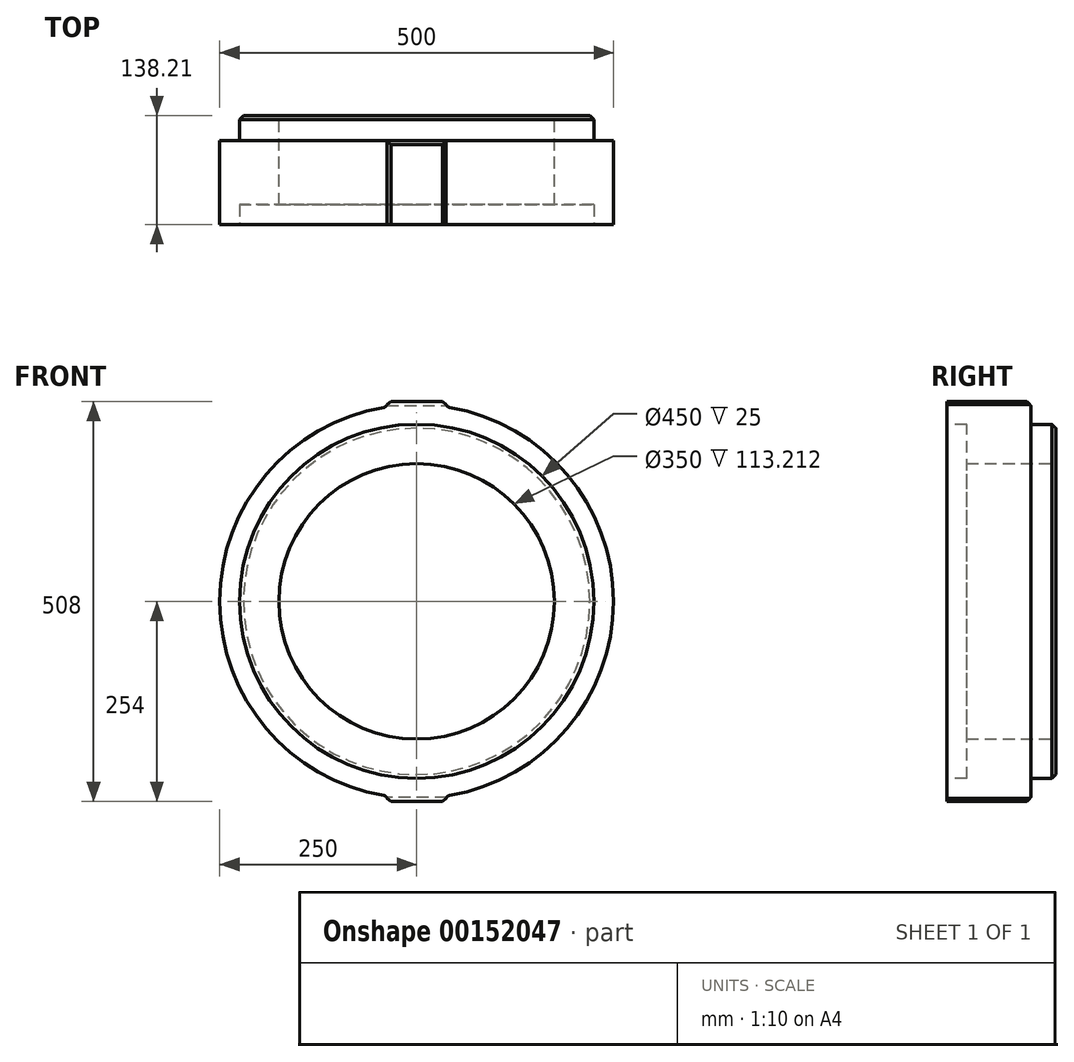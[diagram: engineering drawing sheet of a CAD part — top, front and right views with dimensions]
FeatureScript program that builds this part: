
annotation { "Feature Type Name" : "Feature", "Feature Type Description" : "" }
export const myFeature = defineFeature(function(context is Context, id is Id, definition is map)
    precondition{}
    {
        {
            var Q0;
            Q0=qCreatedBy(makeId("Front.planeOp"),FACE);
            var sketch = newSketch(context, id + "F0", { "sketchPlane" : qUnion([Q0])});
            skArc(sketch, "E0", {"start": v(37.5, -247.17) * mm, "mid": v(250, 0) * mm, "end": v(37.5, 247.17) * mm});
            skLineSegment(sketch, "E1.bottom", {"start": v(37.5, 254) * mm, "end": v(-37.5, 254) * mm});
            skLineSegment(sketch, "E1.top", {"start": v(37.5, -254) * mm, "end": v(-37.5, -254) * mm});
            skLineSegment(sketch, "E1.left", {"start": v(37.5, 254) * mm, "end": v(37.5, 247.17) * mm});
            skLineSegment(sketch, "E1.right", {"start": v(-37.5, 254) * mm, "end": v(-37.5, 247.17) * mm});
            skCircle(sketch, "E2", {"center": v(0, 0) * mm, "radius": 175 * mm});
            skLineSegment(sketch, "E3.trimOffspring", {"start": v(37.5, -247.17) * mm, "end": v(37.5, -254) * mm});
            skLineSegment(sketch, "E4.trimOffspring", {"start": v(-37.5, -247.17) * mm, "end": v(-37.5, -254) * mm});
            skArc(sketch, "E5.trimOffspring", {"start": v(-37.5, 247.17) * mm, "mid": v(-250, 0) * mm, "end": v(-37.5, -247.17) * mm});
            skSolve(sketch);
        }
        {
            var Q0;
            Q0 = qSketchRegion(id + "F0", true);
            extrude(context, id + "F1", {"entities" : qUnion([Q0]), "depth" : 150 * mm});
        }
        {
            var Q0;
            Q0=makeQuery(id+"F1.opExtrude","CAP_FACE",FACE,{"disambiguationData":[OSD([sQuery(id+"F0.wireOp",EDGE,"E0"),sQuery(id+"F0.wireOp",EDGE,"E1.bottom"),sQuery(id+"F0.wireOp",EDGE,"E1.top"),sQuery(id+"F0.wireOp",EDGE,"E1.left"),sQuery(id+"F0.wireOp",EDGE,"E1.right"),sQuery(id+"F0.wireOp",EDGE,"E2"),sQuery(id+"F0.wireOp",EDGE,"E3.trimOffspring"),sQuery(id+"F0.wireOp",EDGE,"E4.trimOffspring"),sQuery(id+"F0.wireOp",EDGE,"E5.trimOffspring")])],"isStart":false});
            var sketch = newSketch(context, id + "F2", { "sketchPlane" : qUnion([Q0])});
            skCircle(sketch, "E6", {"center": v(0, 0) * mm, "radius": 225 * mm});
            skCircle(sketch, "E7", {"center": v(0, 0) * mm, "radius": 175 * mm});
            skSolve(sketch);
        }
        {
            var Q0;
            Q0 = qSketchRegion(id + "F2", true);
            extrude(context, id + "F3", {"entities" : qUnion([Q0]), "operationType" : NewBodyOperationType.REMOVE, "oppositeDirection" : true, "depth" : 25 * mm});
        }
        {
            var Q0;
            Q0=makeQuery(id+"F1.opExtrude","CAP_FACE",FACE,{"disambiguationData":[OSD([sQuery(id+"F0.wireOp",EDGE,"E0"),sQuery(id+"F0.wireOp",EDGE,"E1.bottom"),sQuery(id+"F0.wireOp",EDGE,"E1.top"),sQuery(id+"F0.wireOp",EDGE,"E1.left"),sQuery(id+"F0.wireOp",EDGE,"E1.right"),sQuery(id+"F0.wireOp",EDGE,"E2"),sQuery(id+"F0.wireOp",EDGE,"E3.trimOffspring"),sQuery(id+"F0.wireOp",EDGE,"E4.trimOffspring"),sQuery(id+"F0.wireOp",EDGE,"E5.trimOffspring")])],"isStart":true});
            var sketch = newSketch(context, id + "F4", { "sketchPlane" : qUnion([Q0])});
            skCircle(sketch, "E8", {"center": v(0, 0) * mm, "radius": 175 * mm});
            skCircle(sketch, "E9", {"center": v(0, 0) * mm, "radius": 225 * mm});
            skSolve(sketch);
        }
        {
            var Q0;
            Q0 = qSketchRegion(id + "F4", true);
            extrude(context, id + "F5", {"entities" : qUnion([Q0]), "operationType" : NewBodyOperationType.ADD, "depth" : 32 * mm});
        }
        {
            var Q0;
            Q0=makeQuery(id+"F5.opExtrude","CAP_EDGE",EDGE,{"disambiguationData":[OSD([sQuery(id+"F4.wireOp",EDGE,"E9")])],"isStart":false});
            chamfer(context, id + "F6", {"entities" : qUnion([Q0]), "width" : 5 * mm, "tangentPropagation" : true});
        }
        {
            var Q0;
            Q0=makeQuery(id+"F1.opExtrude","SWEPT_EDGE",EDGE,{"disambiguationData":[OSD([sQuery(id+"F0.wireOp",EDGE,"E1.right"),sQuery(id+"F0.wireOp",EDGE,"E5.trimOffspring")])]});
            var Q1;
            Q1=makeQuery(id+"F1.opExtrude","SWEPT_EDGE",EDGE,{"disambiguationData":[OSD([sQuery(id+"F0.wireOp",EDGE,"E0"),sQuery(id+"F0.wireOp",EDGE,"E1.left")])]});
            var Q2;
            Q2=makeQuery(id+"F1.opExtrude","SWEPT_EDGE",EDGE,{"disambiguationData":[OSD([sQuery(id+"F0.wireOp",EDGE,"E4.trimOffspring"),sQuery(id+"F0.wireOp",EDGE,"E5.trimOffspring")])]});
            var Q3;
            Q3=makeQuery(id+"F1.opExtrude","SWEPT_EDGE",EDGE,{"disambiguationData":[OSD([sQuery(id+"F0.wireOp",EDGE,"E0"),sQuery(id+"F0.wireOp",EDGE,"E3.trimOffspring")])]});
            fillet(context, id + "F7", {"entities" : qUnion([Q0, Q1, Q2, Q3]), "radius" : 5 * mm, "tangentPropagation" : true, "allowEdgeOverflow" : false});
        }
        {
            var Q0;
            Q0=makeQuery(id+"F3.boolean.opBoolean","COPY",FACE,{"derivedFrom":makeQuery(id+"F3.opExtrude","CAP_FACE",FACE,{"disambiguationData":[OSD([sQuery(id+"F2.wireOp",EDGE,"E6"),sQuery(id+"F2.wireOp",EDGE,"E7")])],"isStart":false})});
            extrude(context, id + "F8", {"entities" : qUnion([Q0]), "operationType" : NewBodyOperationType.REMOVE, "oppositeDirection" : true, "depth" : 43.8 * mm});
        }
        {
            var Q0;
            Q0=makeQuery(id+"F1.opExtrude","CAP_FACE",FACE,{"disambiguationData":[OSD([sQuery(id+"F0.wireOp",EDGE,"E0"),sQuery(id+"F0.wireOp",EDGE,"E1.bottom"),sQuery(id+"F0.wireOp",EDGE,"E1.top"),sQuery(id+"F0.wireOp",EDGE,"E1.left"),sQuery(id+"F0.wireOp",EDGE,"E1.right"),sQuery(id+"F0.wireOp",EDGE,"E2"),sQuery(id+"F0.wireOp",EDGE,"E3.trimOffspring"),sQuery(id+"F0.wireOp",EDGE,"E4.trimOffspring"),sQuery(id+"F0.wireOp",EDGE,"E5.trimOffspring")])],"isStart":false});
            extrude(context, id + "F9", {"entities" : qUnion([Q0]), "operationType" : NewBodyOperationType.REMOVE, "oppositeDirection" : true, "depth" : 43.8 * mm});
        }
        {
            var Q0;
            Q0=makeQuery(id+"F1.opExtrude","SWEPT_EDGE",EDGE,{"disambiguationData":[OSD([sQuery(id+"F0.wireOp",EDGE,"E1.bottom"),sQuery(id+"F0.wireOp",EDGE,"E1.right")])]});
            var Q1;
            Q1=makeQuery(id+"F1.opExtrude","SWEPT_EDGE",EDGE,{"disambiguationData":[OSD([sQuery(id+"F0.wireOp",EDGE,"E1.bottom"),sQuery(id+"F0.wireOp",EDGE,"E1.left")])]});
            var Q2;
            Q2=makeQuery(id+"F1.opExtrude","CAP_EDGE",EDGE,{"disambiguationData":[OSD([sQuery(id+"F0.wireOp",EDGE,"E1.bottom")])],"isStart":true});
            var Q3;
            Q3=makeQuery(id+"F9.boolean.opBoolean","COPY",EDGE,{"derivedFrom":makeQuery(id+"F9.opExtrude","CAP_EDGE",EDGE,{"disambiguationData":[OSD([sQuery(id+"F0.wireOp",EDGE,"E1.bottom")])],"isStart":false})});
            chamfer(context, id + "F10", {"entities" : qUnion([Q0, Q1, Q2, Q3]), "width" : 5 * mm, "tangentPropagation" : true});
        }
        {
            var Q0;
            Q0=makeQuery(id+"F1.opExtrude","SWEPT_EDGE",EDGE,{"disambiguationData":[OSD([sQuery(id+"F0.wireOp",EDGE,"E1.top"),sQuery(id+"F0.wireOp",EDGE,"E4.trimOffspring")])]});
            var Q1;
            Q1=makeQuery(id+"F1.opExtrude","SWEPT_EDGE",EDGE,{"disambiguationData":[OSD([sQuery(id+"F0.wireOp",EDGE,"E1.top"),sQuery(id+"F0.wireOp",EDGE,"E3.trimOffspring")])]});
            var Q2;
            Q2=makeQuery(id+"F9.boolean.opBoolean","COPY",EDGE,{"derivedFrom":makeQuery(id+"F9.opExtrude","CAP_EDGE",EDGE,{"disambiguationData":[OSD([sQuery(id+"F0.wireOp",EDGE,"E1.top")])],"isStart":false})});
            var Q3;
            Q3=makeQuery(id+"F1.opExtrude","CAP_EDGE",EDGE,{"disambiguationData":[OSD([sQuery(id+"F0.wireOp",EDGE,"E1.top")])],"isStart":true});
            chamfer(context, id + "F11", {"entities" : qUnion([Q0, Q1, Q2, Q3]), "width" : 5 * mm, "tangentPropagation" : true});
        }
    });
